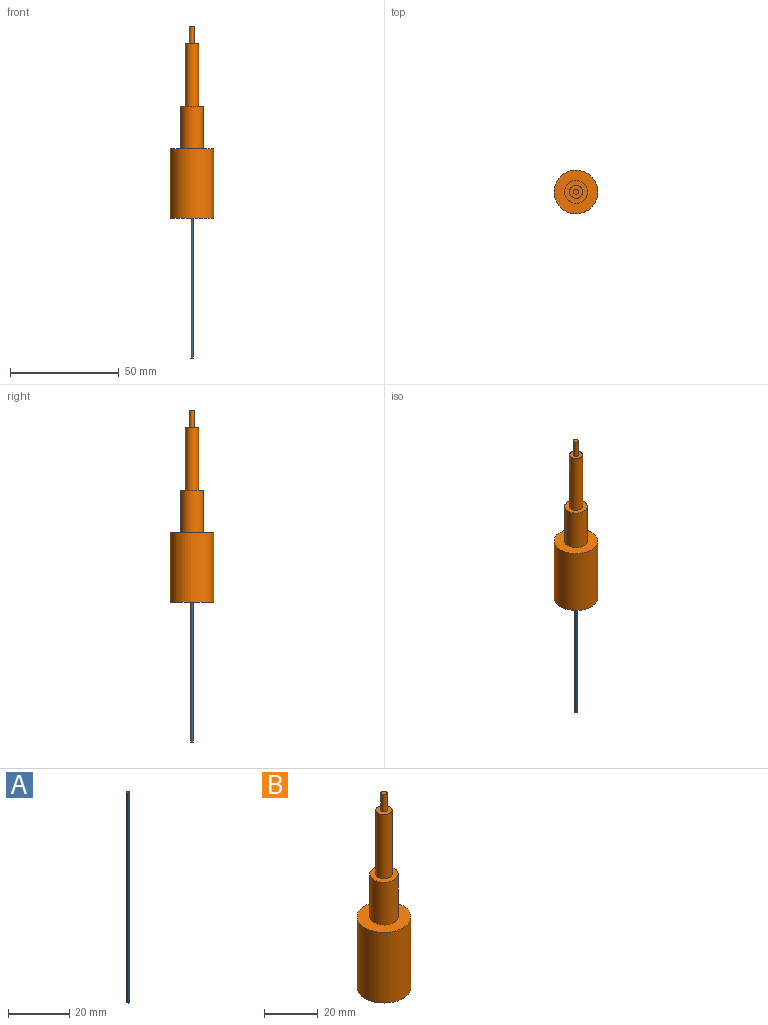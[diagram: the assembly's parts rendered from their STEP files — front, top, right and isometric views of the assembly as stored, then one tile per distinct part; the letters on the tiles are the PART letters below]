
ASSEMBLY  parts=2 mates=1
PART A: 3 faces, bbox 1.2x1.2x84 mm
  f0: cylinder r=0.6mm len=84mm, axis (0,0,-1), area 316.7mm2, adj f1,f2
  f1: plane 1.2x1.2mm, normal (0,0,1), area 1.1mm2, adj f0
  f2: plane 1.2x1.2mm, normal (0,0,-1), area 1.1mm2, adj f0
PART B: 11 faces, bbox 20x20x88.3 mm
  f0: cylinder r=10mm len=32mm, axis (0,0,-1), area 2010.6mm2, adj f1,f2
  f1: plane 20x20mm, normal (0,0,1), area 227.6mm2, adj f0,f3
  f2: plane 20x20mm, normal (0,0,-1), area 313mm2, adj f0,f9
  f3: cylinder r=5.25mm len=19.4mm, axis (0,0,-1), area 639.9mm2, adj f1,f4
  f4: plane 10.5x10.5mm, normal (0,0,1), area 58.3mm2, adj f3,f5
  f5: cylinder r=3mm len=29mm, axis (0,0,-1), area 546.6mm2, adj f4,f6
  f6: plane 6x6mm, normal (0,0,1), area 24.1mm2, adj f5,f7
  f7: cylinder r=1.15mm len=7.9mm, axis (0,0,-1), area 57.1mm2, adj f6,f8
  f8: plane 2.3x2.3mm, normal (0,0,1), area 4.2mm2, adj f7
  f9: cylinder r=0.6mm len=20mm, axis (0,0,-1), area 75.4mm2, adj f2,f10
  f10: plane 1.2x1.2mm, normal (0,0,-1), area 1.1mm2, adj f9
PLACE A rot(axis=(1,0,0),180deg) t=(-10.78,16.31,9.65)mm
PLACE B t=(-10.78,16.31,-10.35)mm
MATE fastened A.f0 <-> B.f9  axis (0,0,1) through (-10.78,16.31,9.65)mm
